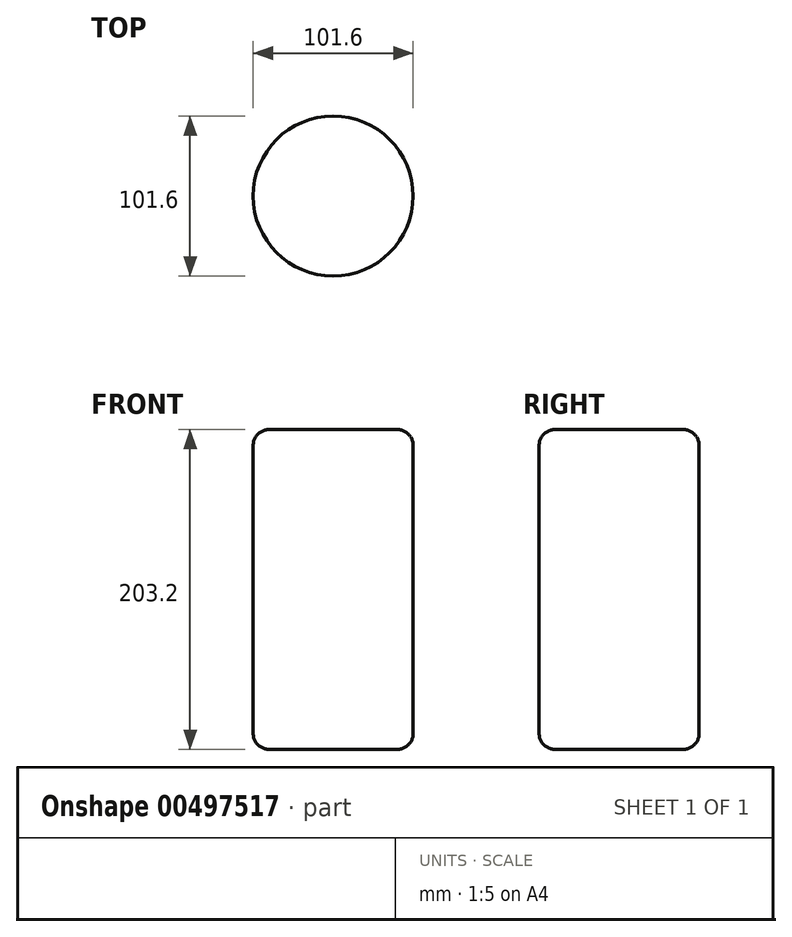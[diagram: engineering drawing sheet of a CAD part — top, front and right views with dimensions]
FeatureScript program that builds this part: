
annotation { "Feature Type Name" : "Feature", "Feature Type Description" : "" }
export const myFeature = defineFeature(function(context is Context, id is Id, definition is map)
    precondition{}
    {
        {
            var Q0;
            Q0=qCreatedBy(makeId("Top.planeOp"),FACE);
            var sketch = newSketch(context, id + "F0", { "sketchPlane" : qUnion([Q0])});
            skCircle(sketch, "E0", {"center": v(0, 0) * mm, "radius": 50.8 * mm});
            skSolve(sketch);
        }
        {
            var Q0;
            Q0 = qSketchRegion(id + "F0", true);
            extrude(context, id + "F1", {"entities" : qUnion([Q0]), "endBound" : BoundingType.SYMMETRIC, "depth" : 203.2 * mm});
        }
        {
            var Q0;
            Q0=makeQuery(id+"F1.opExtrude","CAP_FACE",FACE,{"disambiguationData":[OSD([sQuery(id+"F0.wireOp",EDGE,"E0")])],"isStart":true});
            var Q1;
            Q1=makeQuery(id+"F1.opExtrude","CAP_FACE",FACE,{"disambiguationData":[OSD([sQuery(id+"F0.wireOp",EDGE,"E0")])],"isStart":false});
            fillet(context, id + "F2", {"entities" : qUnion([Q0, Q1]), "radius" : 10.16 * mm, "tangentPropagation" : true, "allowEdgeOverflow" : false});
        }
    });
